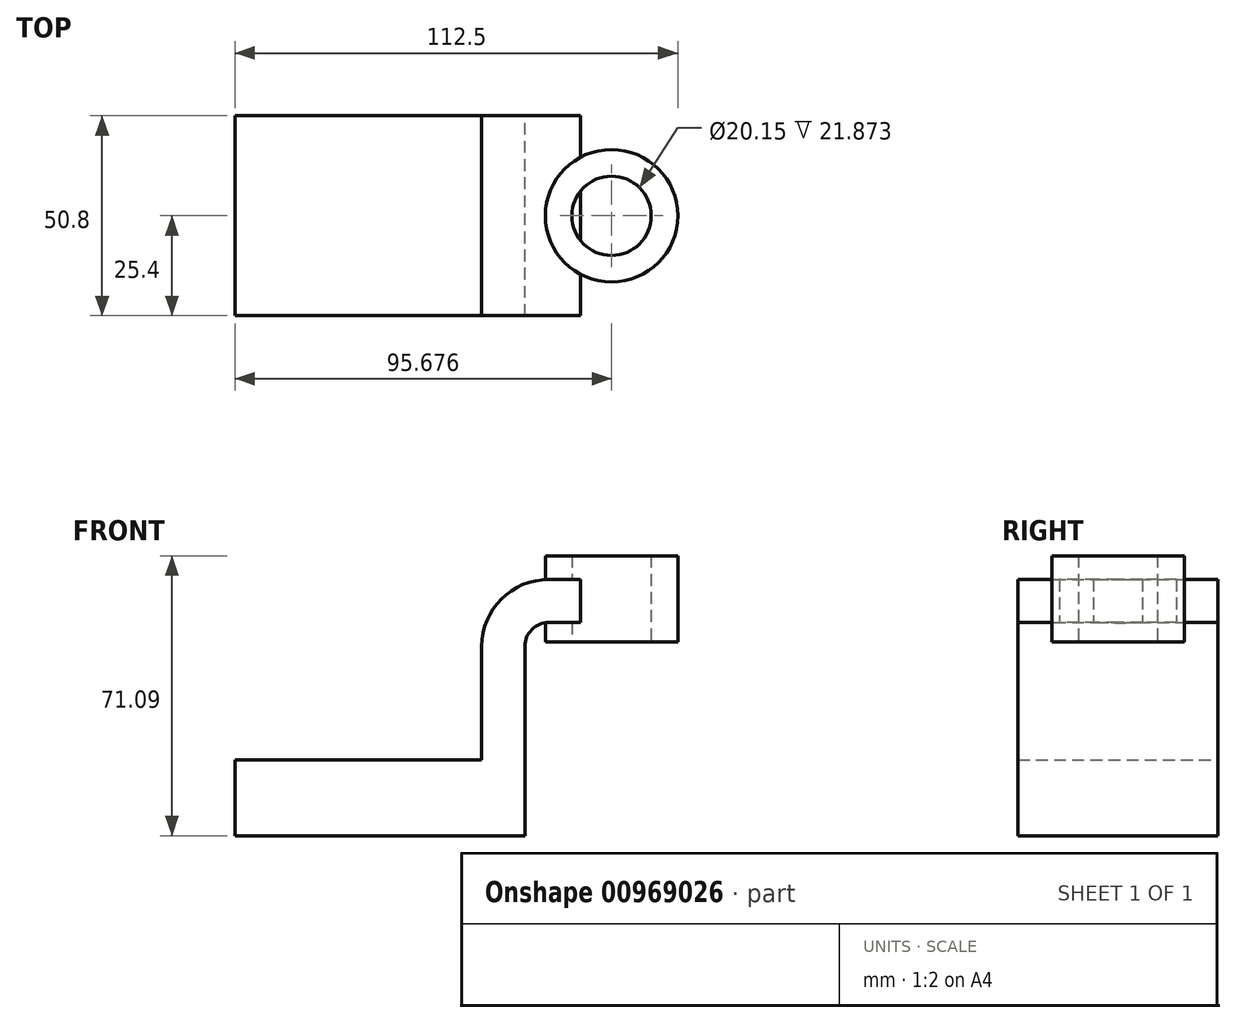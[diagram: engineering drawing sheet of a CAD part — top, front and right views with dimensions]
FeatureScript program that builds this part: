
annotation { "Feature Type Name" : "Feature", "Feature Type Description" : "" }
export const myFeature = defineFeature(function(context is Context, id is Id, definition is map)
    precondition{}
    {
        {
            var Q0;
            Q0=qCreatedBy(makeId("Front.planeOp"),FACE);
            var sketch = newSketch(context, id + "F0", { "sketchPlane" : qUnion([Q0])});
            skLineSegment(sketch, "E0.bottom", {"start": v(36.82, 9.64) * mm, "end": v(-36.82, 9.64) * mm});
            skLineSegment(sketch, "E0.top", {"start": v(36.82, -9.64) * mm, "end": v(-36.82, -9.64) * mm});
            skLineSegment(sketch, "E0.left", {"start": v(36.82, 9.64) * mm, "end": v(36.82, -9.64) * mm});
            skLineSegment(sketch, "E0.right", {"start": v(-36.82, 9.64) * mm, "end": v(-36.82, -9.64) * mm});
            skPoint(sketch, "E0.middle", {"position": v(0, 0) * mm});
            skLineSegment(sketch, "E1.bottom", {"start": v(50.93, 39.57) * mm, "end": v(75.68, 39.57) * mm});
            skLineSegment(sketch, "E1.top", {"start": v(50.93, 61.45) * mm, "end": v(75.68, 61.45) * mm});
            skLineSegment(sketch, "E1.left", {"start": v(50.93, 39.57) * mm, "end": v(50.93, 61.45) * mm});
            skLineSegment(sketch, "E1.right", {"start": v(75.68, 39.57) * mm, "end": v(75.68, 61.45) * mm});
            skPoint(sketch, "E1.middle", {"position": v(63.3, 50.5) * mm});
            skLineSegment(sketch, "E2", {"start": v(36.82, 9.64) * mm, "end": v(36.82, 38.42) * mm});
            skArc(sketch, "E3", {"start": v(36.82, 38.42) * mm, "mid": v(38.6, 42.73) * mm, "end": v(42.92, 44.52) * mm});
            skLineSegment(sketch, "E4", {"start": v(42.92, 44.52) * mm, "end": v(63.89, 44.52) * mm});
            skLineSegment(sketch, "E5.0", {"start": v(42.92, 55.46) * mm, "end": v(63.89, 55.46) * mm});
            skArc(sketch, "E5.1", {"start": v(25.89, 38.42) * mm, "mid": v(30.88, 50.47) * mm, "end": v(42.92, 55.46) * mm});
            skLineSegment(sketch, "E5.2", {"start": v(25.89, 9.64) * mm, "end": v(25.89, 38.42) * mm});
            skFitSpline(sketch, "E6", {"points": [v(-36.82, 9.64) * mm, v(42.92, 55.46) * mm], "startDerivative": vector(24.08, 86.34) * mm, "endDerivative": vector(101.18, -7.6) * mm});
            skLineSegment(sketch, "E7", {"start": v(63.89, 44.52) * mm, "end": v(63.89, 55.46) * mm});
            skLineSegment(sketch, "E8", {"start": v(68.93, 39.57) * mm, "end": v(68.93, 61.45) * mm});
            skLineSegment(sketch, "E9", {"start": v(58.86, 39.57) * mm, "end": v(58.86, 61.45) * mm});
            skSolve(sketch);
        }
        {
            var Q0;
            Q0=makeQuery(id+"F0.imprint","IMPRINT",FACE,{"disambiguationData":[TD([[makeQuery(id+"F0.imprint","IMPRINT",EDGE,{"derivedFrom":sQuery(id+"F0.wireOp",EDGE,"E0.top")}),-1.0]])]});
            extrude(context, id + "F1", {"entities" : qUnion([Q0]), "endBound" : BoundingType.SYMMETRIC, "depth" : 50.8 * mm, "offsetDistance" : 25.4 * mm});
        }
        {
            var Q0;
            Q0=makeQuery(id+"F0.imprint","IMPRINT",FACE,{"disambiguationData":[TD([[makeQuery(id+"F0.imprint","IMPRINT",EDGE,{"derivedFrom":sQuery(id+"F0.wireOp",EDGE,"E5.1")}),1.0]])]});
            extrude(context, id + "F2", {"entities" : qUnion([Q0]), "operationType" : NewBodyOperationType.ADD, "endBound" : BoundingType.SYMMETRIC, "depth" : 12.7 * mm, "offsetDistance" : 25.4 * mm});
        }
        {
            var Q0;
            {var subQ1=sQuery(id+"F0.wireOp",EDGE,"E2");Q0=makeQuery(id+"F0.imprint","IMPRINT",FACE,{"disambiguationData":[TD([[makeQuery(id+"F0.imprint","IMPRINT",EDGE,{"derivedFrom":subQ1}),1.0]])]});}
            extrude(context, id + "F3", {"entities" : qUnion([Q0]), "operationType" : NewBodyOperationType.ADD, "endBound" : BoundingType.SYMMETRIC, "depth" : 50.8 * mm, "offsetDistance" : 25.4 * mm});
        }
        {
            var Q0;
            {var subQ0=sQuery(id+"F0.wireOp",EDGE,"E1.right");Q0=makeQuery(id+"F0.imprint","IMPRINT",FACE,{"disambiguationData":[TD([[makeQuery(id+"F0.imprint","IMPRINT",EDGE,{"derivedFrom":subQ0}),1.0]])]});}
            var Q1;
            Q1=sQuery(id+"F0.wireOp",EDGE,"E9");
            revolve(context, id + "F4", {"operationType" : NewBodyOperationType.ADD, "surfaceOperationType" : NewSurfaceOperationType.NEW, "entities" : qUnion([Q0]), "axis" : qUnion([Q1]), "revolveType" : RevolveType.FULL});
        }
    });
